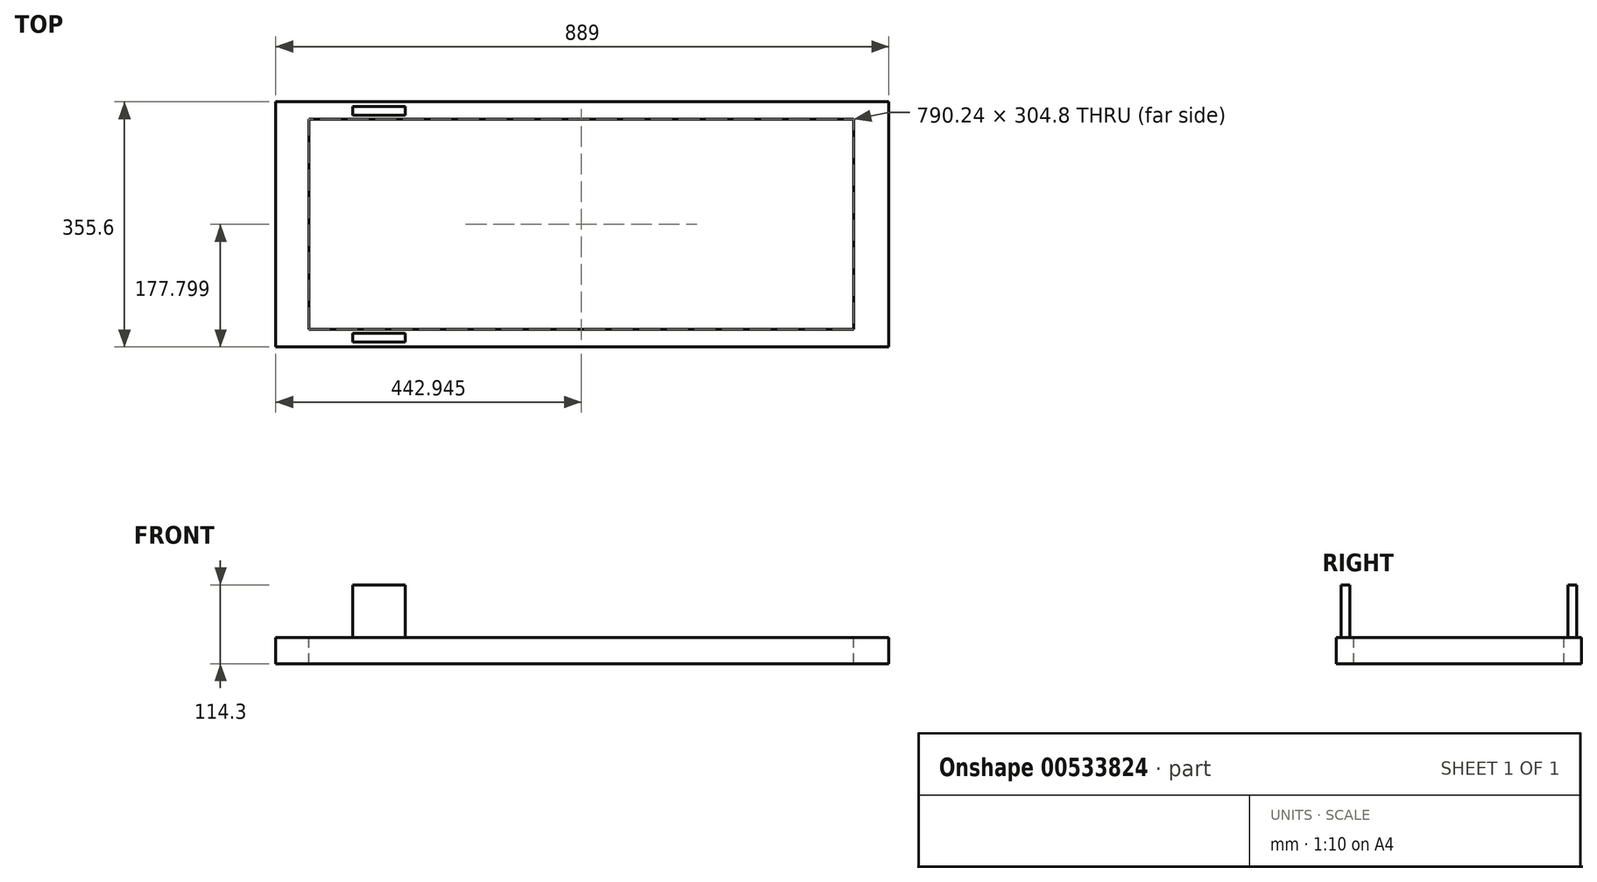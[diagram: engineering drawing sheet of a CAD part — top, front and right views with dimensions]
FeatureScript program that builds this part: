
annotation { "Feature Type Name" : "Feature", "Feature Type Description" : "" }
export const myFeature = defineFeature(function(context is Context, id is Id, definition is map)
    precondition{}
    {
        {
            var Q0;
            Q0=qCreatedBy(makeId("Top.planeOp"),FACE);
            var sketch = newSketch(context, id + "F0", { "sketchPlane" : qUnion([Q0])});
            skLineSegment(sketch, "E0.bottom", {"start": v(-442.94, 74.72) * mm, "end": v(446.06, 74.72) * mm});
            skLineSegment(sketch, "E0.top", {"start": v(-442.94, -280.88) * mm, "end": v(446.06, -280.88) * mm});
            skPoint(sketch, "E1.start.orphan", {"position": v(-442.94, 0) * mm});
            skLineSegment(sketch, "E2", {"start": v(-442.94, 74.72) * mm, "end": v(-442.94, -280.88) * mm});
            skLineSegment(sketch, "E3", {"start": v(446.06, 74.72) * mm, "end": v(446.06, -280.88) * mm});
            skSolve(sketch);
        }
        {
            var Q0;
            Q0 = qSketchRegion(id + "F0", true);
            extrude(context, id + "F1", {"entities" : qUnion([Q0]), "depth" : 38.1 * mm, "offsetDistance" : 25.4 * mm});
        }
        {
            var Q0;
            Q0=makeQuery(id+"F1.opExtrude","CAP_FACE",FACE,{"disambiguationData":[OSD([sQuery(id+"F0.wireOp",EDGE,"E0.bottom"),sQuery(id+"F0.wireOp",EDGE,"E0.top"),sQuery(id+"F0.wireOp",EDGE,"E0.left"),sQuery(id+"F0.wireOp",EDGE,"E0.right")])],"isStart":false});
            var sketch = newSketch(context, id + "F2", { "sketchPlane" : qUnion([Q0])});
            skLineSegment(sketch, "E4.bottom", {"start": v(-395.12, 49.32) * mm, "end": v(395.13, 49.32) * mm});
            skLineSegment(sketch, "E4.top", {"start": v(-395.12, -255.48) * mm, "end": v(395.13, -255.48) * mm});
            skLineSegment(sketch, "E4.left", {"start": v(-395.12, 49.32) * mm, "end": v(-395.12, -255.48) * mm});
            skLineSegment(sketch, "E4.right", {"start": v(395.13, 49.32) * mm, "end": v(395.13, -255.48) * mm});
            skLineSegment(sketch, "E5", {"start": v(-395.12, 0) * mm, "end": v(395.13, 0) * mm, "construction": true});
            skPoint(sketch, "E6.orphan", {"position": v(-404.97, 0) * mm});
            skSolve(sketch);
        }
        {
            var Q0;
            Q0 = qSketchRegion(id + "F2", true);
            extrude(context, id + "F3", {"entities" : qUnion([Q0]), "operationType" : NewBodyOperationType.REMOVE, "oppositeDirection" : true, "depth" : 170.18 * mm, "offsetDistance" : 25.4 * mm});
        }
        {
            var Q0;
            Q0=makeQuery(id+"F1.opExtrude","CAP_FACE",FACE,{"disambiguationData":[OSD([sQuery(id+"F0.wireOp",EDGE,"E0.bottom"),sQuery(id+"F0.wireOp",EDGE,"E0.top"),sQuery(id+"F0.wireOp",EDGE,"E0.left"),sQuery(id+"F0.wireOp",EDGE,"E0.right")])],"isStart":false});
            var sketch = newSketch(context, id + "F4", { "sketchPlane" : qUnion([Q0])});
            skLineSegment(sketch, "E7.bottom", {"start": v(-331.74, -261.07) * mm, "end": v(-255.54, -261.07) * mm});
            skLineSegment(sketch, "E7.top", {"start": v(-331.74, -273.77) * mm, "end": v(-255.54, -273.77) * mm});
            skLineSegment(sketch, "E7.left", {"start": v(-331.74, -261.07) * mm, "end": v(-331.74, -273.77) * mm});
            skLineSegment(sketch, "E7.right", {"start": v(-255.54, -261.07) * mm, "end": v(-255.54, -273.77) * mm});
            skLineSegment(sketch, "E8.bottom", {"start": v(-331.74, 54.9) * mm, "end": v(-255.54, 54.9) * mm});
            skLineSegment(sketch, "E8.top", {"start": v(-331.74, 67.6) * mm, "end": v(-255.54, 67.6) * mm});
            skLineSegment(sketch, "E8.left", {"start": v(-331.74, 54.9) * mm, "end": v(-331.74, 67.6) * mm});
            skLineSegment(sketch, "E8.right", {"start": v(-255.54, 54.9) * mm, "end": v(-255.54, 67.6) * mm});
            skSolve(sketch);
        }
        {
            var Q0;
            Q0=makeQuery(id+"F4.imprint","IMPRINT",FACE,{"disambiguationData":[TD([[makeQuery(id+"F4.imprint","IMPRINT",EDGE,{"derivedFrom":sQuery(id+"F4.wireOp",EDGE,"E7.bottom")}),-1.0]])]});
            var Q1;
            Q1=makeQuery(id+"F4.imprint","IMPRINT",FACE,{"disambiguationData":[TD([[makeQuery(id+"F4.imprint","IMPRINT",EDGE,{"derivedFrom":sQuery(id+"F4.wireOp",EDGE,"E8.bottom")}),1.0]])]});
            extrude(context, id + "F5", {"entities" : qUnion([Q0, Q1]), "operationType" : NewBodyOperationType.ADD, "depth" : 76.2 * mm, "offsetDistance" : 25.4 * mm});
        }
    });
